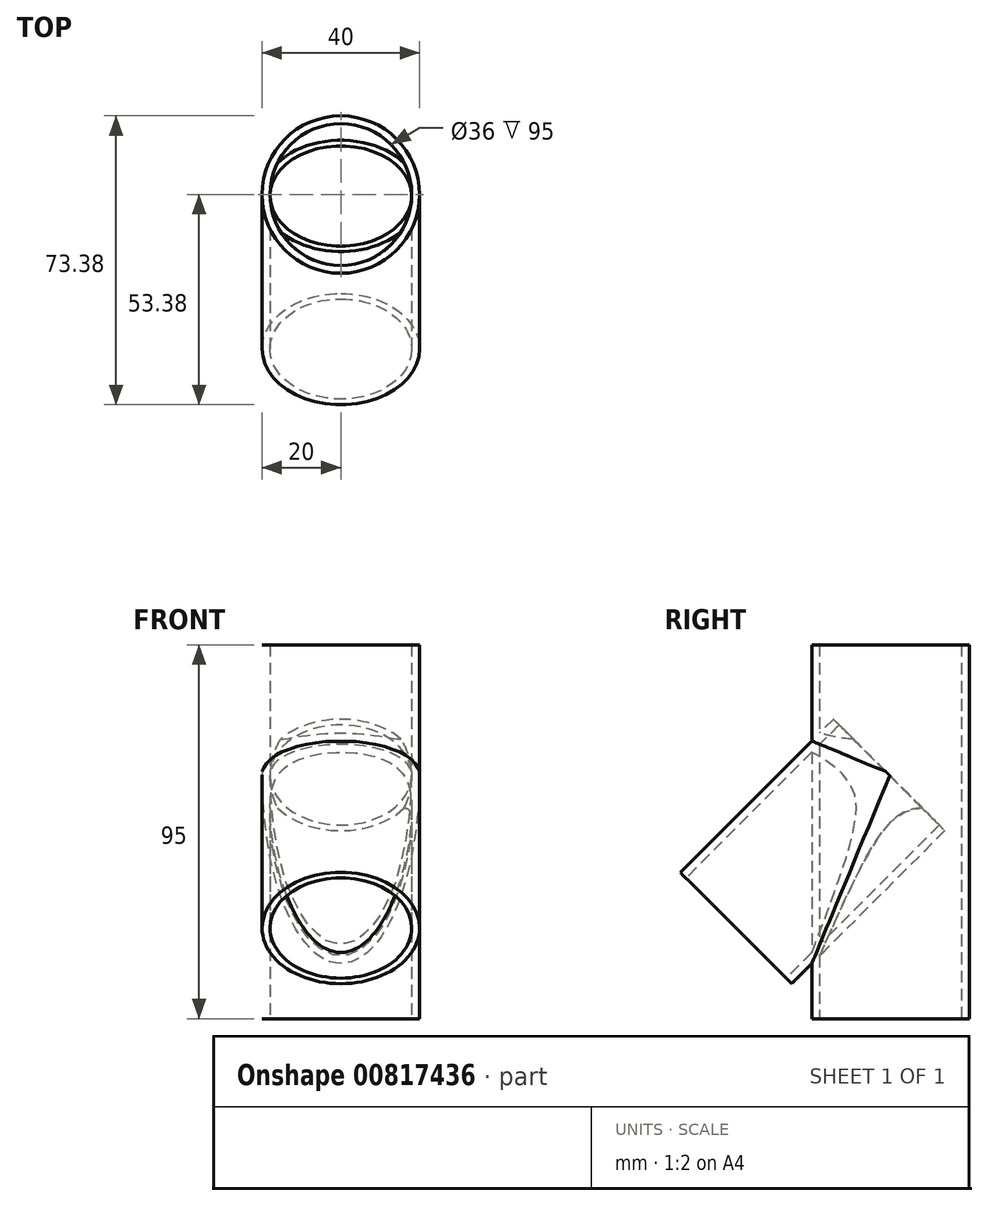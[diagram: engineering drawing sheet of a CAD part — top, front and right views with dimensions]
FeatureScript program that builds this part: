
annotation { "Feature Type Name" : "Feature", "Feature Type Description" : "" }
export const myFeature = defineFeature(function(context is Context, id is Id, definition is map)
    precondition{}
    {
        {
            var Q0;
            Q0=qCreatedBy(makeId("Top.planeOp"),FACE);
            var sketch = newSketch(context, id + "F0", { "sketchPlane" : qUnion([Q0])});
            skCircle(sketch, "E0", {"center": v(0, 0) * mm, "radius": 20 * mm});
            skCircle(sketch, "E1", {"center": v(0, 0) * mm, "radius": 18 * mm});
            skSolve(sketch);
        }
        {
            var Q0;
            Q0=makeQuery(id+"F0.imprint","IMPRINT",FACE,{"disambiguationData":[TD([[makeQuery(id+"F0.imprint","IMPRINT",EDGE,{"derivedFrom":sQuery(id+"F0.wireOp",EDGE,"E0")}),1.0]])]});
            extrude(context, id + "F1", {"entities" : qUnion([Q0]), "depth" : 90 * mm, "offsetDistance" : 25 * mm, "hasSecondDirection" : true, "secondDirectionOppositeDirection" : true, "secondDirectionDepth" : 5 * mm});
        }
        {
            var Q0;
            Q0=qCreatedBy(makeId("Top.planeOp"),FACE);
            var sketch = newSketch(context, id + "F2", { "sketchPlane" : qUnion([Q0])});
            skLineSegment(sketch, "E2", {"start": v(-100.16, 0) * mm, "end": v(102.3, 0) * mm, "construction": true});
            skSolve(sketch);
        }
        {
            var Q0;
            Q0=sQuery(id+"F2.wireOp",EDGE,"E2");
            var Q1;
            Q1=makeQuery(id+"F1.opExtrude","CAP_EDGE",EDGE,{"disambiguationData":[OSD([sQuery(id+"F0.wireOp",EDGE,"E1")])],"isStart":true});
            cPlane(context, id + "F3", {"entities" : qUnion([Q0, Q1]), "cplaneType" : CPlaneType.LINE_ANGLE, "offset" : 25 * mm, "angle" : 45 * degree, "width" : 150 * mm, "height" : 150 * mm});
        }
        {
            var Q0;
            Q0=qCreatedBy(id+"F3.planeOp",FACE);
            var sketch = newSketch(context, id + "F4", { "sketchPlane" : qUnion([Q0])});
            skCircle(sketch, "E3", {"center": v(0, 40.5) * mm, "radius": 20 * mm});
            skCircle(sketch, "E4", {"center": v(0, 40.5) * mm, "radius": 18 * mm});
            skSolve(sketch);
        }
        {
            var Q0;
            Q0=makeQuery(id+"F4.imprint","IMPRINT",FACE,{"disambiguationData":[TD([[makeQuery(id+"F4.imprint","IMPRINT",EDGE,{"derivedFrom":sQuery(id+"F4.wireOp",EDGE,"E3")}),1.0]])]});
            extrude(context, id + "F5", {"entities" : qUnion([Q0]), "operationType" : NewBodyOperationType.ADD, "oppositeDirection" : true, "depth" : 40 * mm, "offsetDistance" : 25 * mm, "hasSecondDirection" : true, "secondDirectionOppositeDirection" : false, "secondDirectionDepth" : 15 * mm});
        }
    });
